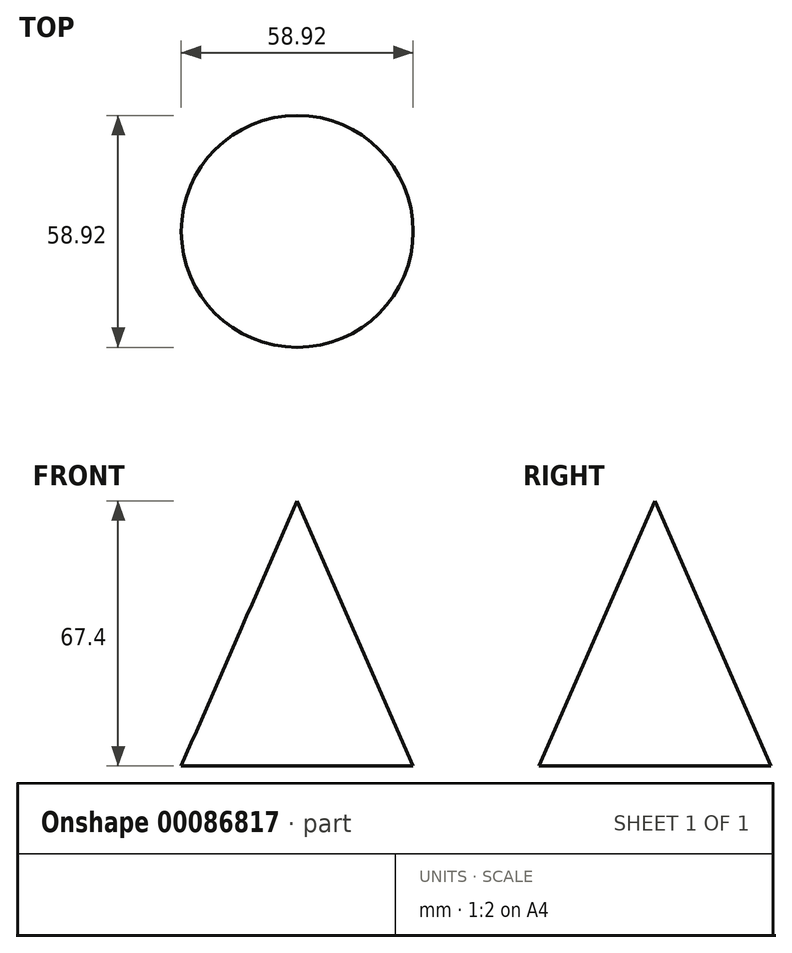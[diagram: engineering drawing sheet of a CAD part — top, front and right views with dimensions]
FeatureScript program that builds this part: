
annotation { "Feature Type Name" : "Feature", "Feature Type Description" : "" }
export const myFeature = defineFeature(function(context is Context, id is Id, definition is map)
    precondition{}
    {
        {
            var Q0;
            Q0=qCreatedBy(makeId("Front.planeOp"),FACE);
            var sketch = newSketch(context, id + "F0", { "sketchPlane" : qUnion([Q0])});
            skLineSegment(sketch, "E0", {"start": v(0, 0) * mm, "end": v(29.46, 0) * mm});
            skLineSegment(sketch, "E1", {"start": v(29.46, 0) * mm, "end": v(0, 67.4) * mm});
            skLineSegment(sketch, "E2", {"start": v(0, 67.4) * mm, "end": v(0, 0) * mm});
            skSolve(sketch);
        }
        {
            var Q0;
            Q0 = qSketchRegion(id + "F0", true);
            var Q1;
            Q1=sQuery(id+"F0.wireOp",EDGE,"E2");
            revolve(context, id + "F1", {"entities" : qUnion([Q0]), "axis" : qUnion([Q1]), "revolveType" : RevolveType.FULL});
        }
    });
